# Revit family: PUZ-ZM60VHA2(-ET,ER)
name_source: partatom
category: Mechanical Equipment
revit_build: Autodesk Revit 2018 (Build: 20181015_0930(x64)
units: mm (PartAtom-declared; Revit-internal decimal feet)

## family parameters
Always vertical = Yes
Cut with Voids When Loaded = No
OmniClass Number = 23.75.00.00
OmniClass Title = Climate Control (HVAC)
Part Type = Normal
Room Calculation Point = No
Round Connector Dimension = Use Diameter
Shared = No
Work Plane-Based = No

## types (1)
- PUZ-ZM60VHA2(-ET,ER)
    Compressor = Hermetic
    Compressor Model = SVB172FFUM1
    Compressor Motor Output (kW) = 1.25
    Compressor Protection devices = HP switch, Comp. surface thermo, Discharge thermo, Over current detection
    Compressor Starter type = Inverter
    Connection method  Indoor side = Flared
    Connection method Outdoor side = Flared
    Cooling Sound pressure level (SPL) (dB) = 49
    Crankcase heater = -
    Defrost method = Reverse cycle
    Depth (in) = 13+1-3/16
    Depth (mm)_ = 300+25
    Equip_No. = 0
    External Finish = Munsell 3Y 7.8/1.1
    Fan Airflow (m3/min) (CFM) = 55 (1940)
    Fan Motor Output (kW) = 0.074
    Fan No. = 1
    Fan drive = Propeller fan
    Gas pipe_diameter (in) = 5/8
    Gas pipe_diameter (mm) = 15.88 mm  [stored 0.0520997 ft]
    Heat exchanger = Plate fin coill
    Heating Sound pressure level (SPL) (dB) = 47
    Height (in) = 37-1/8
    Height (mm) = 943 mm  [stored 3.09383 ft]
    Hertz = 50 Hz
    Liquid pipe_diameter (in) = 3/8
    Liquid pipe_diameter (mm) = 9.52 mm
    Manufacturer = Mitsubishi Electric Corporation
    Maxmum current (A) = 19 A
    Model = PUZ-ZM60VHA2(-ET,ER)
PUZ-ZM60VHA2(-ET,ER)
    Phase = 1
    Refrigerant Oil (Model) (L) = 0.70 (FW68S)
    Refrigerant Piping Height difference Between the indoor and outdoor unit(m) = Maximum 30
    Refrigerant Piping length Between the indoor and outdoor unit(m) = Maximum 55
    Refrigerant charge (kg) = 2.8
    Refrigerant charge (lb) = 6.2
    Refrigerant control = Linear Expansion Valve
    Refrigerant type = R32
    SerialNumber = 0
    Space View = Yes
    Subcategory = HVAC
    TagNumber = 0
    URL = http://www.mitsubishielectric.com
    Unit Weight (kg) = 67
    Unit Weight (lbS) = 148
    Voltage = 230 V
    Width (in) = 37-13/32
    Width (mm) = 950 mm  [stored 3.1168 ft]

note: [stored X ft] marks values corroborated as IEEE doubles in the binary element streams (Revit-internal decimal feet)

## geometry (parser evidence)
native form markers: Blend x14, Sweep x2
no freeform markers — native parametric forms only
